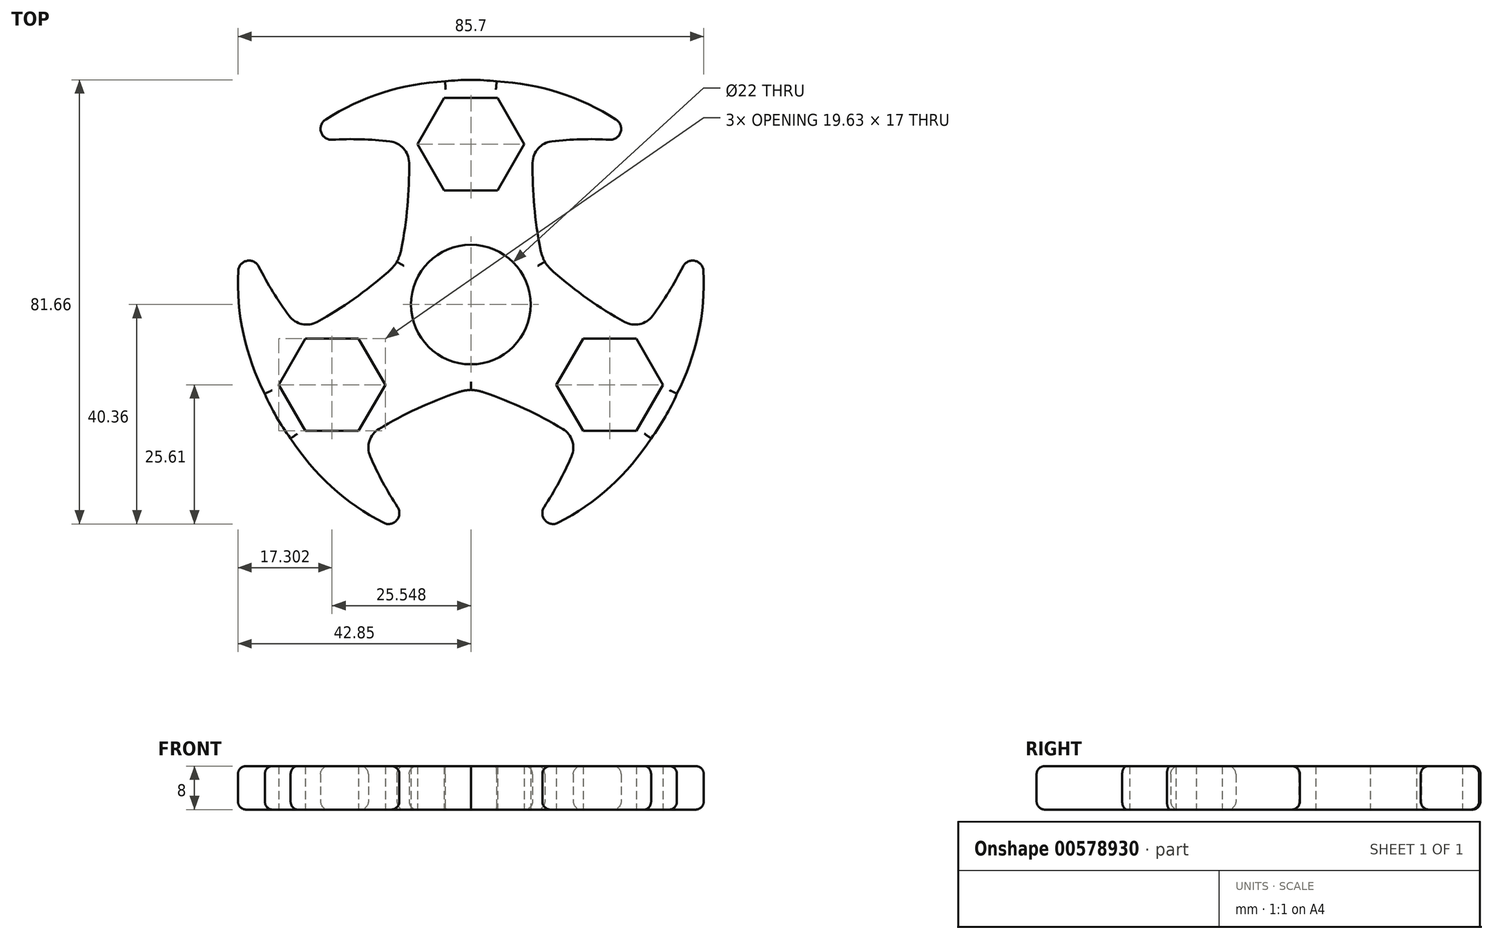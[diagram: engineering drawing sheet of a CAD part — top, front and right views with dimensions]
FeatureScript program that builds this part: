
annotation { "Feature Type Name" : "Feature", "Feature Type Description" : "" }
export const myFeature = defineFeature(function(context is Context, id is Id, definition is map)
    precondition{}
    {
        {
            var Q0;
            Q0=qCreatedBy(makeId("Top.planeOp"),FACE);
            var sketch = newSketch(context, id + "F0", { "sketchPlane" : qUnion([Q0])});
            skCircle(sketch, "E0", {"center": v(0, 0) * mm, "radius": 11 * mm});
            skCircle(sketch, "E1.cCircle", {"center": v(0, 29.5) * mm, "radius": 8.5 * mm, "construction": true});
            skLineSegment(sketch, "E1.0", {"start": v(4.9, 21) * mm, "end": v(-4.9, 21) * mm});
            skLineSegment(sketch, "E1.1", {"start": v(-4.9, 21) * mm, "end": v(-9.81, 29.5) * mm});
            skLineSegment(sketch, "E1.2", {"start": v(-9.81, 29.5) * mm, "end": v(-4.9, 38) * mm});
            skLineSegment(sketch, "E1.3", {"start": v(-4.9, 38) * mm, "end": v(4.9, 38) * mm});
            skLineSegment(sketch, "E1.4", {"start": v(4.9, 38) * mm, "end": v(9.81, 29.5) * mm});
            skLineSegment(sketch, "E1.5", {"start": v(9.81, 29.5) * mm, "end": v(4.9, 21) * mm});
            skPoint(sketch, "E1.0.midPoint", {"position": v(0, 21) * mm});
            skArc(sketch, "E2", {"start": v(11.37, 26.08) * mm, "mid": v(11.66, 18.1) * mm, "end": v(12.79, 10.19) * mm});
            skArc(sketch, "E3.MirrorCS", {"start": v(-11.37, 26.08) * mm, "mid": v(-11.66, 18.1) * mm, "end": v(-12.79, 10.19) * mm});
            skPoint(sketch, "E4.orphan", {"position": v(7, 12.12) * mm});
            skPoint(sketch, "E5.orphan", {"position": v(-7, 12.12) * mm});
            skPoint(sketch, "E6.visualSharp", {"position": v(-13.42, 7.27) * mm});
            skArc(sketch, "E6.filletArc", {"start": v(-13.6, 7.85) * mm, "mid": v(-13.11, 9) * mm, "end": v(-12.79, 10.19) * mm});
            skPoint(sketch, "E7.visualSharp", {"position": v(13.42, 7.27) * mm});
            skArc(sketch, "E7.filletArc", {"start": v(12.79, 10.19) * mm, "mid": v(13.11, 9) * mm, "end": v(13.6, 7.85) * mm});
            skCircle(sketch, "E8.1.0", {"center": v(-25.55, -14.75) * mm, "radius": 8.5 * mm, "construction": true});
            skPoint(sketch, "E8.1.2", {"position": v(-18.19, -10.5) * mm});
            skLineSegment(sketch, "E8.1.3", {"start": v(-35.36, -14.75) * mm, "end": v(-30.46, -6.25) * mm});
            skLineSegment(sketch, "E8.1.4", {"start": v(-30.46, -23.25) * mm, "end": v(-35.36, -14.75) * mm});
            skLineSegment(sketch, "E8.1.5", {"start": v(-20.64, -6.25) * mm, "end": v(-15.73, -14.75) * mm});
            skLineSegment(sketch, "E8.1.6", {"start": v(-30.46, -6.25) * mm, "end": v(-20.64, -6.25) * mm});
            skLineSegment(sketch, "E8.1.7", {"start": v(-15.73, -14.75) * mm, "end": v(-20.64, -23.25) * mm});
            skLineSegment(sketch, "E8.1.8", {"start": v(-20.64, -23.25) * mm, "end": v(-30.46, -23.25) * mm});
            skArc(sketch, "E8.1.9", {"start": v(-28.27, -3.2) * mm, "mid": v(-21.5, 1.04) * mm, "end": v(-15.22, 5.98) * mm});
            skArc(sketch, "E8.1.10", {"start": v(-16.9, -22.88) * mm, "mid": v(-9.85, -19.14) * mm, "end": v(-2.43, -16.17) * mm});
            skArc(sketch, "E8.1.11", {"start": v(0, -15.7) * mm, "mid": v(-1.23, -15.85) * mm, "end": v(-2.43, -16.17) * mm});
            skArc(sketch, "E8.1.12", {"start": v(-15.22, 5.98) * mm, "mid": v(-14.34, 6.86) * mm, "end": v(-13.6, 7.85) * mm});
            skCircle(sketch, "E8.2.0", {"center": v(25.55, -14.75) * mm, "radius": 8.5 * mm, "construction": true});
            skPoint(sketch, "E8.2.2", {"position": v(18.19, -10.5) * mm});
            skLineSegment(sketch, "E8.2.3", {"start": v(30.46, -23.25) * mm, "end": v(20.64, -23.25) * mm});
            skLineSegment(sketch, "E8.2.4", {"start": v(35.36, -14.75) * mm, "end": v(30.46, -23.25) * mm});
            skLineSegment(sketch, "E8.2.5", {"start": v(15.73, -14.75) * mm, "end": v(20.64, -6.25) * mm});
            skLineSegment(sketch, "E8.2.6", {"start": v(20.64, -23.25) * mm, "end": v(15.73, -14.75) * mm});
            skLineSegment(sketch, "E8.2.7", {"start": v(20.64, -6.25) * mm, "end": v(30.46, -6.25) * mm});
            skLineSegment(sketch, "E8.2.8", {"start": v(30.46, -6.25) * mm, "end": v(35.36, -14.75) * mm});
            skArc(sketch, "E8.2.9", {"start": v(16.9, -22.88) * mm, "mid": v(9.85, -19.14) * mm, "end": v(2.43, -16.17) * mm});
            skArc(sketch, "E8.2.10", {"start": v(28.27, -3.2) * mm, "mid": v(21.5, 1.04) * mm, "end": v(15.22, 5.98) * mm});
            skArc(sketch, "E8.2.11", {"start": v(13.6, 7.85) * mm, "mid": v(14.34, 6.86) * mm, "end": v(15.22, 5.98) * mm});
            skArc(sketch, "E8.2.12", {"start": v(2.43, -16.17) * mm, "mid": v(1.23, -15.85) * mm, "end": v(0, -15.7) * mm});
            skPoint(sketch, "E9.orphan", {"position": v(12.31, 11) * mm});
            skPoint(sketch, "E10.orphan", {"position": v(15.7, 5.16) * mm});
            skPoint(sketch, "E11.orphan", {"position": v(3.38, -16.17) * mm});
            skPoint(sketch, "E12.orphan", {"position": v(-3.38, -16.17) * mm});
            skPoint(sketch, "E13.orphan", {"position": v(-12.31, 11) * mm});
            skPoint(sketch, "E14.orphan", {"position": v(-15.7, 5.16) * mm});
            skPoint(sketch, "E15.second.point", {"position": v(32.57, 29.5) * mm});
            skPoint(sketch, "E15.third.point", {"position": v(20.04, 35.13) * mm});
            skArc(sketch, "E16", {"start": v(26.73, 33.98) * mm, "mid": v(16.2, 38.95) * mm, "end": v(4.74, 41.02) * mm});
            skArc(sketch, "E17", {"start": v(25.54, 30.3) * mm, "mid": v(20.21, 30.37) * mm, "end": v(14.9, 29.99) * mm});
            skArc(sketch, "E18.filletArc", {"start": v(25.54, 30.3) * mm, "mid": v(27.55, 31.68) * mm, "end": v(26.73, 33.98) * mm});
            skArc(sketch, "E19.MirrorCS", {"start": v(-26.73, 33.98) * mm, "mid": v(-16.2, 38.95) * mm, "end": v(-4.75, 41.02) * mm});
            skArc(sketch, "E20.MirrorCS", {"start": v(-25.54, 30.3) * mm, "mid": v(-20.21, 30.37) * mm, "end": v(-14.9, 29.99) * mm});
            skArc(sketch, "E21.MirrorCS", {"start": v(-25.54, 30.3) * mm, "mid": v(-27.55, 31.68) * mm, "end": v(-26.73, 33.98) * mm});
            skArc(sketch, "E22", {"start": v(4.74, 41.02) * mm, "mid": v(0, 41.3) * mm, "end": v(-4.75, 41.02) * mm});
            skPoint(sketch, "E23.orphan", {"position": v(0, 41) * mm});
            skArc(sketch, "E24.1.0", {"start": v(-16.06, -40.14) * mm, "mid": v(-25.63, -33.5) * mm, "end": v(-33.15, -24.63) * mm});
            skArc(sketch, "E24.1.1", {"start": v(-13.47, -37.27) * mm, "mid": v(-13.66, -39.7) * mm, "end": v(-16.06, -40.14) * mm});
            skArc(sketch, "E24.1.2", {"start": v(-13.47, -37.27) * mm, "mid": v(-16.2, -32.7) * mm, "end": v(-18.52, -27.9) * mm});
            skArc(sketch, "E24.1.3", {"start": v(-39, 6.97) * mm, "mid": v(-36.41, 2.32) * mm, "end": v(-33.42, -2.09) * mm});
            skArc(sketch, "E24.1.4", {"start": v(-39, 6.97) * mm, "mid": v(-41.21, 8.02) * mm, "end": v(-42.8, 6.16) * mm});
            skArc(sketch, "E24.1.5", {"start": v(-42.8, 6.16) * mm, "mid": v(-41.83, -5.45) * mm, "end": v(-37.9, -16.4) * mm});
            skArc(sketch, "E24.1.6", {"start": v(-37.9, -16.4) * mm, "mid": v(-35.76, -20.65) * mm, "end": v(-33.15, -24.63) * mm});
            skArc(sketch, "E24.2.0", {"start": v(42.8, 6.16) * mm, "mid": v(41.83, -5.44) * mm, "end": v(37.9, -16.4) * mm});
            skArc(sketch, "E24.2.1", {"start": v(39, 6.97) * mm, "mid": v(41.21, 8.02) * mm, "end": v(42.8, 6.16) * mm});
            skArc(sketch, "E24.2.2", {"start": v(39, 6.97) * mm, "mid": v(36.41, 2.32) * mm, "end": v(33.42, -2.09) * mm});
            skArc(sketch, "E24.2.3", {"start": v(13.47, -37.27) * mm, "mid": v(16.2, -32.7) * mm, "end": v(18.52, -27.9) * mm});
            skArc(sketch, "E24.2.4", {"start": v(13.47, -37.27) * mm, "mid": v(13.66, -39.7) * mm, "end": v(16.06, -40.14) * mm});
            skArc(sketch, "E24.2.5", {"start": v(16.06, -40.14) * mm, "mid": v(25.63, -33.5) * mm, "end": v(33.16, -24.62) * mm});
            skArc(sketch, "E24.2.6", {"start": v(33.16, -24.62) * mm, "mid": v(35.77, -20.64) * mm, "end": v(37.9, -16.4) * mm});
            skPoint(sketch, "E25.visualSharp", {"position": v(-11.5, 29.5) * mm});
            skArc(sketch, "E25.filletArc", {"start": v(-11.37, 26.08) * mm, "mid": v(-12.4, 28.7) * mm, "end": v(-14.9, 29.99) * mm});
            skPoint(sketch, "E26.visualSharp", {"position": v(11.5, 29.5) * mm});
            skArc(sketch, "E26.filletArc", {"start": v(14.9, 29.99) * mm, "mid": v(12.4, 28.7) * mm, "end": v(11.37, 26.08) * mm});
            skPoint(sketch, "E27.visualSharp", {"position": v(31.3, -4.8) * mm});
            skArc(sketch, "E27.filletArc", {"start": v(28.27, -3.2) * mm, "mid": v(31.06, -3.61) * mm, "end": v(33.42, -2.09) * mm});
            skPoint(sketch, "E28.visualSharp", {"position": v(19.8, -24.7) * mm});
            skArc(sketch, "E28.filletArc", {"start": v(18.52, -27.9) * mm, "mid": v(18.66, -25.1) * mm, "end": v(16.9, -22.88) * mm});
            skPoint(sketch, "E29.visualSharp", {"position": v(-19.8, -24.7) * mm});
            skArc(sketch, "E29.filletArc", {"start": v(-16.9, -22.88) * mm, "mid": v(-18.66, -25.1) * mm, "end": v(-18.52, -27.9) * mm});
            skPoint(sketch, "E30.visualSharp", {"position": v(-31.3, -4.8) * mm});
            skArc(sketch, "E30.filletArc", {"start": v(-33.42, -2.09) * mm, "mid": v(-31.06, -3.61) * mm, "end": v(-28.27, -3.2) * mm});
            skSolve(sketch);
        }
        {
            var Q0;
            Q0 = qSketchRegion(id + "F0", true);
            extrude(context, id + "F1", {"entities" : qUnion([Q0]), "depth" : 8 * mm, "offsetDistance" : 25 * mm});
        }
        {
            var Q0;
            Q0=makeQuery(id+"F1.opExtrude","CAP_EDGE",EDGE,{"disambiguationData":[OSD([sQuery(id+"F0.wireOp",EDGE,"E3.MirrorCS")])],"isStart":false});
            var Q1;
            Q1=makeQuery(id+"F1.opExtrude","CAP_EDGE",EDGE,{"disambiguationData":[OSD([sQuery(id+"F0.wireOp",EDGE,"E6.filletArc")])],"isStart":false});
            var Q2;
            Q2=makeQuery(id+"F1.opExtrude","CAP_EDGE",EDGE,{"disambiguationData":[OSD([sQuery(id+"F0.wireOp",EDGE,"E8.1.12")])],"isStart":false});
            var Q3;
            Q3=makeQuery(id+"F1.opExtrude","CAP_EDGE",EDGE,{"disambiguationData":[OSD([sQuery(id+"F0.wireOp",EDGE,"E8.1.9")])],"isStart":false});
            var Q4;
            Q4=makeQuery(id+"F1.opExtrude","CAP_EDGE",EDGE,{"disambiguationData":[OSD([sQuery(id+"F0.wireOp",EDGE,"E30.filletArc")])],"isStart":false});
            var Q5;
            Q5=makeQuery(id+"F1.opExtrude","CAP_EDGE",EDGE,{"disambiguationData":[OSD([sQuery(id+"F0.wireOp",EDGE,"E24.1.3")])],"isStart":false});
            var Q6;
            Q6=makeQuery(id+"F1.opExtrude","CAP_EDGE",EDGE,{"disambiguationData":[OSD([sQuery(id+"F0.wireOp",EDGE,"E24.1.4")])],"isStart":false});
            var Q7;
            Q7=makeQuery(id+"F1.opExtrude","CAP_EDGE",EDGE,{"disambiguationData":[OSD([sQuery(id+"F0.wireOp",EDGE,"E24.1.5")])],"isStart":false});
            var Q8;
            Q8=makeQuery(id+"F1.opExtrude","CAP_EDGE",EDGE,{"disambiguationData":[OSD([sQuery(id+"F0.wireOp",EDGE,"E24.1.6")])],"isStart":false});
            var Q9;
            Q9=makeQuery(id+"F1.opExtrude","CAP_EDGE",EDGE,{"disambiguationData":[OSD([sQuery(id+"F0.wireOp",EDGE,"E24.1.0")])],"isStart":false});
            var Q10;
            Q10=makeQuery(id+"F1.opExtrude","CAP_EDGE",EDGE,{"disambiguationData":[OSD([sQuery(id+"F0.wireOp",EDGE,"E24.1.2")])],"isStart":false});
            var Q11;
            Q11=makeQuery(id+"F1.opExtrude","CAP_EDGE",EDGE,{"disambiguationData":[OSD([sQuery(id+"F0.wireOp",EDGE,"E29.filletArc")])],"isStart":false});
            var Q12;
            Q12=makeQuery(id+"F1.opExtrude","CAP_EDGE",EDGE,{"disambiguationData":[OSD([sQuery(id+"F0.wireOp",EDGE,"E8.1.10")])],"isStart":false});
            var Q13;
            Q13=makeQuery(id+"F1.opExtrude","CAP_EDGE",EDGE,{"disambiguationData":[OSD([sQuery(id+"F0.wireOp",EDGE,"E8.2.12")])],"isStart":false});
            var Q14;
            Q14=makeQuery(id+"F1.opExtrude","CAP_EDGE",EDGE,{"disambiguationData":[OSD([sQuery(id+"F0.wireOp",EDGE,"E8.1.11")])],"isStart":false});
            var Q15;
            Q15=makeQuery(id+"F1.opExtrude","CAP_EDGE",EDGE,{"disambiguationData":[OSD([sQuery(id+"F0.wireOp",EDGE,"E8.2.9")])],"isStart":false});
            var Q16;
            Q16=makeQuery(id+"F1.opExtrude","CAP_EDGE",EDGE,{"disambiguationData":[OSD([sQuery(id+"F0.wireOp",EDGE,"E28.filletArc")])],"isStart":false});
            var Q17;
            Q17=makeQuery(id+"F1.opExtrude","CAP_EDGE",EDGE,{"disambiguationData":[OSD([sQuery(id+"F0.wireOp",EDGE,"E24.2.3")])],"isStart":false});
            var Q18;
            Q18=makeQuery(id+"F1.opExtrude","CAP_EDGE",EDGE,{"disambiguationData":[OSD([sQuery(id+"F0.wireOp",EDGE,"E24.2.4")])],"isStart":false});
            var Q19;
            Q19=makeQuery(id+"F1.opExtrude","CAP_EDGE",EDGE,{"disambiguationData":[OSD([sQuery(id+"F0.wireOp",EDGE,"E24.2.5")])],"isStart":false});
            var Q20;
            Q20=makeQuery(id+"F1.opExtrude","CAP_EDGE",EDGE,{"disambiguationData":[OSD([sQuery(id+"F0.wireOp",EDGE,"E24.2.6")])],"isStart":false});
            var Q21;
            Q21=makeQuery(id+"F1.opExtrude","CAP_EDGE",EDGE,{"disambiguationData":[OSD([sQuery(id+"F0.wireOp",EDGE,"E24.2.0")])],"isStart":false});
            var Q22;
            Q22=makeQuery(id+"F1.opExtrude","CAP_EDGE",EDGE,{"disambiguationData":[OSD([sQuery(id+"F0.wireOp",EDGE,"E24.2.1")])],"isStart":false});
            var Q23;
            Q23=makeQuery(id+"F1.opExtrude","CAP_EDGE",EDGE,{"disambiguationData":[OSD([sQuery(id+"F0.wireOp",EDGE,"E24.2.2")])],"isStart":false});
            var Q24;
            Q24=makeQuery(id+"F1.opExtrude","CAP_EDGE",EDGE,{"disambiguationData":[OSD([sQuery(id+"F0.wireOp",EDGE,"E27.filletArc")])],"isStart":false});
            var Q25;
            Q25=makeQuery(id+"F1.opExtrude","CAP_EDGE",EDGE,{"disambiguationData":[OSD([sQuery(id+"F0.wireOp",EDGE,"E8.2.10")])],"isStart":false});
            var Q26;
            Q26=makeQuery(id+"F1.opExtrude","CAP_EDGE",EDGE,{"disambiguationData":[OSD([sQuery(id+"F0.wireOp",EDGE,"E8.2.11")])],"isStart":false});
            var Q27;
            Q27=makeQuery(id+"F1.opExtrude","CAP_EDGE",EDGE,{"disambiguationData":[OSD([sQuery(id+"F0.wireOp",EDGE,"E7.filletArc")])],"isStart":false});
            var Q28;
            Q28=makeQuery(id+"F1.opExtrude","CAP_EDGE",EDGE,{"disambiguationData":[OSD([sQuery(id+"F0.wireOp",EDGE,"E2")])],"isStart":false});
            var Q29;
            Q29=makeQuery(id+"F1.opExtrude","CAP_EDGE",EDGE,{"disambiguationData":[OSD([sQuery(id+"F0.wireOp",EDGE,"E26.filletArc")])],"isStart":false});
            var Q30;
            Q30=makeQuery(id+"F1.opExtrude","CAP_EDGE",EDGE,{"disambiguationData":[OSD([sQuery(id+"F0.wireOp",EDGE,"E17")])],"isStart":false});
            var Q31;
            Q31=makeQuery(id+"F1.opExtrude","CAP_EDGE",EDGE,{"disambiguationData":[OSD([sQuery(id+"F0.wireOp",EDGE,"E18.filletArc")])],"isStart":false});
            var Q32;
            Q32=makeQuery(id+"F1.opExtrude","CAP_EDGE",EDGE,{"disambiguationData":[OSD([sQuery(id+"F0.wireOp",EDGE,"E16")])],"isStart":false});
            var Q33;
            Q33=makeQuery(id+"F1.opExtrude","CAP_EDGE",EDGE,{"disambiguationData":[OSD([sQuery(id+"F0.wireOp",EDGE,"E22")])],"isStart":false});
            var Q34;
            Q34=makeQuery(id+"F1.opExtrude","CAP_EDGE",EDGE,{"disambiguationData":[OSD([sQuery(id+"F0.wireOp",EDGE,"E19.MirrorCS")])],"isStart":false});
            var Q35;
            Q35=makeQuery(id+"F1.opExtrude","CAP_EDGE",EDGE,{"disambiguationData":[OSD([sQuery(id+"F0.wireOp",EDGE,"E20.MirrorCS")])],"isStart":false});
            var Q36;
            Q36=makeQuery(id+"F1.opExtrude","CAP_EDGE",EDGE,{"disambiguationData":[OSD([sQuery(id+"F0.wireOp",EDGE,"E25.filletArc")])],"isStart":false});
            var Q37;
            Q37=makeQuery(id+"F1.opExtrude","CAP_EDGE",EDGE,{"disambiguationData":[OSD([sQuery(id+"F0.wireOp",EDGE,"E21.MirrorCS")])],"isStart":false});
            var Q38;
            Q38=makeQuery(id+"F1.opExtrude","CAP_EDGE",EDGE,{"disambiguationData":[OSD([sQuery(id+"F0.wireOp",EDGE,"E24.1.1")])],"isStart":false});
            fillet(context, id + "F2", {"entities" : qUnion([Q0, Q1, Q2, Q3, Q4, Q5, Q6, Q7, Q8, Q9, Q10, Q11, Q12, Q13, Q14, Q15, Q16, Q17, Q18, Q19, Q20, Q21, Q22, Q23, Q24, Q25, Q26, Q27, Q28, Q29, Q30, Q31, Q32, Q33, Q34, Q35, Q36, Q37, Q38]), "radius" : 1.5 * mm, "tangentPropagation" : true, "allowEdgeOverflow" : false});
        }
        {
            var Q0;
            Q0=makeQuery(id+"F1.opExtrude","CAP_EDGE",EDGE,{"disambiguationData":[OSD([sQuery(id+"F0.wireOp",EDGE,"E24.1.5")])],"isStart":true});
            var Q1;
            Q1=makeQuery(id+"F1.opExtrude","CAP_EDGE",EDGE,{"disambiguationData":[OSD([sQuery(id+"F0.wireOp",EDGE,"E24.1.6")])],"isStart":true});
            var Q2;
            Q2=makeQuery(id+"F1.opExtrude","CAP_EDGE",EDGE,{"disambiguationData":[OSD([sQuery(id+"F0.wireOp",EDGE,"E24.1.1")])],"isStart":true});
            var Q3;
            Q3=makeQuery(id+"F1.opExtrude","CAP_EDGE",EDGE,{"disambiguationData":[OSD([sQuery(id+"F0.wireOp",EDGE,"E29.filletArc")])],"isStart":true});
            var Q4;
            Q4=makeQuery(id+"F1.opExtrude","CAP_EDGE",EDGE,{"disambiguationData":[OSD([sQuery(id+"F0.wireOp",EDGE,"E24.1.2")])],"isStart":true});
            var Q5;
            Q5=makeQuery(id+"F1.opExtrude","CAP_EDGE",EDGE,{"disambiguationData":[OSD([sQuery(id+"F0.wireOp",EDGE,"E8.1.10")])],"isStart":true});
            var Q6;
            Q6=makeQuery(id+"F1.opExtrude","CAP_EDGE",EDGE,{"disambiguationData":[OSD([sQuery(id+"F0.wireOp",EDGE,"E8.1.11")])],"isStart":true});
            var Q7;
            Q7=makeQuery(id+"F1.opExtrude","CAP_EDGE",EDGE,{"disambiguationData":[OSD([sQuery(id+"F0.wireOp",EDGE,"E8.2.9")])],"isStart":true});
            var Q8;
            Q8=makeQuery(id+"F1.opExtrude","CAP_EDGE",EDGE,{"disambiguationData":[OSD([sQuery(id+"F0.wireOp",EDGE,"E28.filletArc")])],"isStart":true});
            var Q9;
            Q9=makeQuery(id+"F1.opExtrude","CAP_EDGE",EDGE,{"disambiguationData":[OSD([sQuery(id+"F0.wireOp",EDGE,"E24.2.3")])],"isStart":true});
            var Q10;
            Q10=makeQuery(id+"F1.opExtrude","CAP_EDGE",EDGE,{"disambiguationData":[OSD([sQuery(id+"F0.wireOp",EDGE,"E24.2.4")])],"isStart":true});
            var Q11;
            Q11=makeQuery(id+"F1.opExtrude","CAP_EDGE",EDGE,{"disambiguationData":[OSD([sQuery(id+"F0.wireOp",EDGE,"E24.2.5")])],"isStart":true});
            var Q12;
            Q12=makeQuery(id+"F1.opExtrude","CAP_EDGE",EDGE,{"disambiguationData":[OSD([sQuery(id+"F0.wireOp",EDGE,"E24.2.6")])],"isStart":true});
            var Q13;
            Q13=makeQuery(id+"F1.opExtrude","CAP_EDGE",EDGE,{"disambiguationData":[OSD([sQuery(id+"F0.wireOp",EDGE,"E24.2.0")])],"isStart":true});
            var Q14;
            Q14=makeQuery(id+"F1.opExtrude","CAP_EDGE",EDGE,{"disambiguationData":[OSD([sQuery(id+"F0.wireOp",EDGE,"E24.2.1")])],"isStart":true});
            var Q15;
            Q15=makeQuery(id+"F1.opExtrude","CAP_EDGE",EDGE,{"disambiguationData":[OSD([sQuery(id+"F0.wireOp",EDGE,"E24.2.2")])],"isStart":true});
            var Q16;
            Q16=makeQuery(id+"F1.opExtrude","CAP_EDGE",EDGE,{"disambiguationData":[OSD([sQuery(id+"F0.wireOp",EDGE,"E27.filletArc")])],"isStart":true});
            var Q17;
            Q17=makeQuery(id+"F1.opExtrude","CAP_EDGE",EDGE,{"disambiguationData":[OSD([sQuery(id+"F0.wireOp",EDGE,"E8.2.10")])],"isStart":true});
            var Q18;
            Q18=makeQuery(id+"F1.opExtrude","CAP_EDGE",EDGE,{"disambiguationData":[OSD([sQuery(id+"F0.wireOp",EDGE,"E8.2.11")])],"isStart":true});
            var Q19;
            Q19=makeQuery(id+"F1.opExtrude","CAP_EDGE",EDGE,{"disambiguationData":[OSD([sQuery(id+"F0.wireOp",EDGE,"E7.filletArc")])],"isStart":true});
            var Q20;
            Q20=makeQuery(id+"F1.opExtrude","CAP_EDGE",EDGE,{"disambiguationData":[OSD([sQuery(id+"F0.wireOp",EDGE,"E2")])],"isStart":true});
            var Q21;
            Q21=makeQuery(id+"F1.opExtrude","CAP_EDGE",EDGE,{"disambiguationData":[OSD([sQuery(id+"F0.wireOp",EDGE,"E26.filletArc")])],"isStart":true});
            var Q22;
            Q22=makeQuery(id+"F1.opExtrude","CAP_EDGE",EDGE,{"disambiguationData":[OSD([sQuery(id+"F0.wireOp",EDGE,"E17")])],"isStart":true});
            var Q23;
            Q23=makeQuery(id+"F1.opExtrude","CAP_EDGE",EDGE,{"disambiguationData":[OSD([sQuery(id+"F0.wireOp",EDGE,"E18.filletArc")])],"isStart":true});
            var Q24;
            Q24=makeQuery(id+"F1.opExtrude","CAP_EDGE",EDGE,{"disambiguationData":[OSD([sQuery(id+"F0.wireOp",EDGE,"E16")])],"isStart":true});
            var Q25;
            Q25=makeQuery(id+"F1.opExtrude","CAP_EDGE",EDGE,{"disambiguationData":[OSD([sQuery(id+"F0.wireOp",EDGE,"E22")])],"isStart":true});
            var Q26;
            Q26=makeQuery(id+"F1.opExtrude","CAP_EDGE",EDGE,{"disambiguationData":[OSD([sQuery(id+"F0.wireOp",EDGE,"E19.MirrorCS")])],"isStart":true});
            var Q27;
            Q27=makeQuery(id+"F1.opExtrude","CAP_EDGE",EDGE,{"disambiguationData":[OSD([sQuery(id+"F0.wireOp",EDGE,"E21.MirrorCS")])],"isStart":true});
            var Q28;
            Q28=makeQuery(id+"F1.opExtrude","CAP_EDGE",EDGE,{"disambiguationData":[OSD([sQuery(id+"F0.wireOp",EDGE,"E20.MirrorCS")])],"isStart":true});
            var Q29;
            Q29=makeQuery(id+"F1.opExtrude","CAP_EDGE",EDGE,{"disambiguationData":[OSD([sQuery(id+"F0.wireOp",EDGE,"E25.filletArc")])],"isStart":true});
            var Q30;
            Q30=makeQuery(id+"F1.opExtrude","CAP_EDGE",EDGE,{"disambiguationData":[OSD([sQuery(id+"F0.wireOp",EDGE,"E3.MirrorCS")])],"isStart":true});
            var Q31;
            Q31=makeQuery(id+"F1.opExtrude","CAP_EDGE",EDGE,{"disambiguationData":[OSD([sQuery(id+"F0.wireOp",EDGE,"E6.filletArc")])],"isStart":true});
            var Q32;
            Q32=makeQuery(id+"F1.opExtrude","CAP_EDGE",EDGE,{"disambiguationData":[OSD([sQuery(id+"F0.wireOp",EDGE,"E8.1.12")])],"isStart":true});
            var Q33;
            Q33=makeQuery(id+"F1.opExtrude","CAP_EDGE",EDGE,{"disambiguationData":[OSD([sQuery(id+"F0.wireOp",EDGE,"E8.1.9")])],"isStart":true});
            var Q34;
            Q34=makeQuery(id+"F1.opExtrude","CAP_EDGE",EDGE,{"disambiguationData":[OSD([sQuery(id+"F0.wireOp",EDGE,"E30.filletArc")])],"isStart":true});
            var Q35;
            Q35=makeQuery(id+"F1.opExtrude","CAP_EDGE",EDGE,{"disambiguationData":[OSD([sQuery(id+"F0.wireOp",EDGE,"E24.1.3")])],"isStart":true});
            var Q36;
            Q36=makeQuery(id+"F1.opExtrude","CAP_EDGE",EDGE,{"disambiguationData":[OSD([sQuery(id+"F0.wireOp",EDGE,"E24.1.4")])],"isStart":true});
            var Q37;
            Q37=makeQuery(id+"F1.opExtrude","CAP_EDGE",EDGE,{"disambiguationData":[OSD([sQuery(id+"F0.wireOp",EDGE,"E24.1.0")])],"isStart":true});
            var Q38;
            Q38=makeQuery(id+"F1.opExtrude","CAP_EDGE",EDGE,{"disambiguationData":[OSD([sQuery(id+"F0.wireOp",EDGE,"E8.2.12")])],"isStart":true});
            fillet(context, id + "F3", {"entities" : qUnion([Q0, Q1, Q2, Q3, Q4, Q5, Q6, Q7, Q8, Q9, Q10, Q11, Q12, Q13, Q14, Q15, Q16, Q17, Q18, Q19, Q20, Q21, Q22, Q23, Q24, Q25, Q26, Q27, Q28, Q29, Q30, Q31, Q32, Q33, Q34, Q35, Q36, Q37, Q38]), "radius" : 1.5 * mm, "tangentPropagation" : true, "allowEdgeOverflow" : false});
        }
    });
